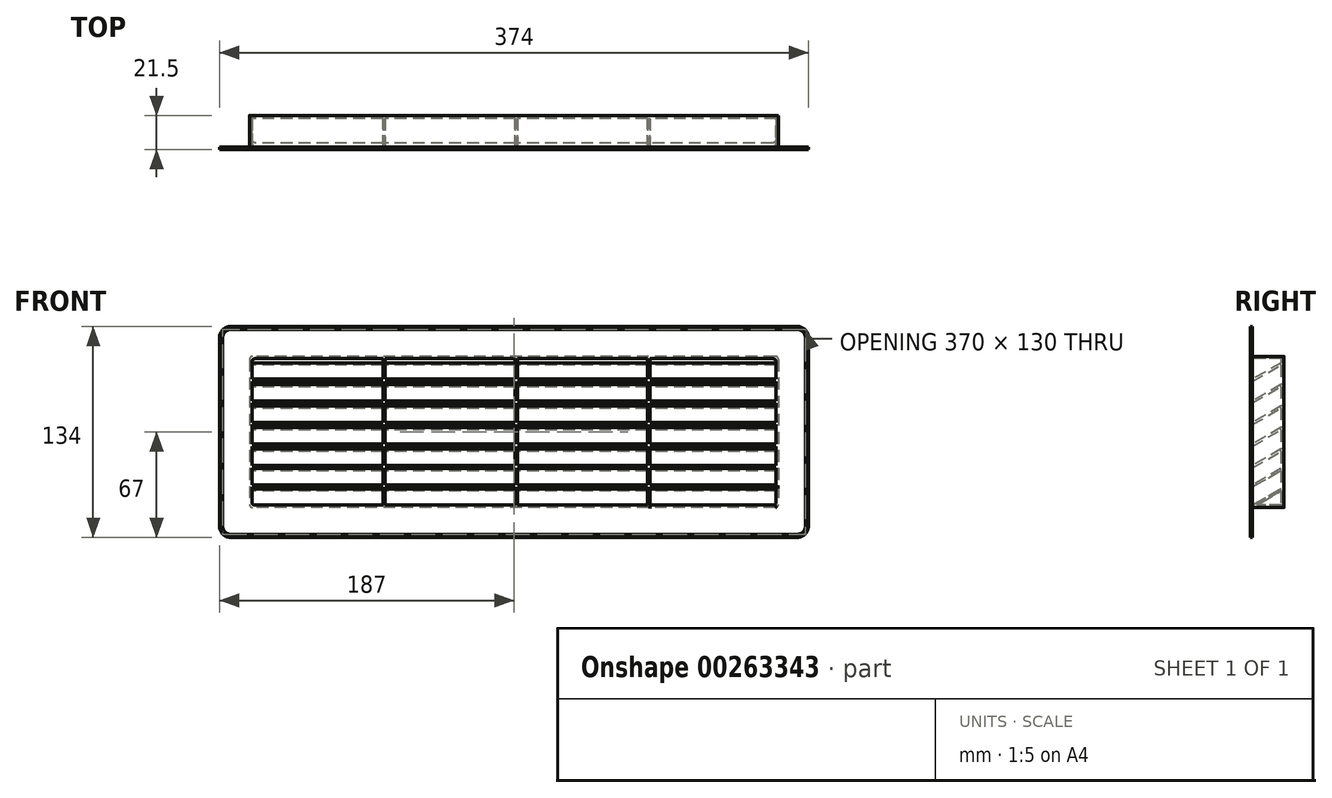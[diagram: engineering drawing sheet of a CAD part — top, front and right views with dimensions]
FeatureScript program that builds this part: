
annotation { "Feature Type Name" : "Feature", "Feature Type Description" : "" }
export const myFeature = defineFeature(function(context is Context, id is Id, definition is map)
    precondition{}
    {
        {
            var Q0;
            Q0=qCreatedBy(makeId("Front.planeOp"),FACE);
            var sketch = newSketch(context, id + "F0", { "sketchPlane" : qUnion([Q0])});
            skLineSegment(sketch, "E0.bottom", {"start": v(-180, 65) * mm, "end": v(180, 65) * mm});
            skLineSegment(sketch, "E0.top", {"start": v(-180, -65) * mm, "end": v(180, -65) * mm});
            skLineSegment(sketch, "E0.left", {"start": v(-185, 60) * mm, "end": v(-185, -60) * mm});
            skLineSegment(sketch, "E0.right", {"start": v(185, 60) * mm, "end": v(185, -60) * mm});
            skPoint(sketch, "E0.middle", {"position": v(0, 0) * mm});
            skPoint(sketch, "E1.visualSharp", {"position": v(-185, 65) * mm});
            skArc(sketch, "E1.filletArc", {"start": v(-180, 65) * mm, "mid": v(-183.54, 63.54) * mm, "end": v(-185, 60) * mm});
            skPoint(sketch, "E2.visualSharp", {"position": v(185, 65) * mm});
            skArc(sketch, "E2.filletArc", {"start": v(185, 60) * mm, "mid": v(183.54, 63.54) * mm, "end": v(180, 65) * mm});
            skPoint(sketch, "E3.visualSharp", {"position": v(185, -65) * mm});
            skArc(sketch, "E3.filletArc", {"start": v(180, -65) * mm, "mid": v(183.54, -63.54) * mm, "end": v(185, -60) * mm});
            skPoint(sketch, "E4.visualSharp", {"position": v(-185, -65) * mm});
            skArc(sketch, "E4.filletArc", {"start": v(-185, -60) * mm, "mid": v(-183.54, -63.54) * mm, "end": v(-180, -65) * mm});
            skSolve(sketch);
        }
        {
            var Q0;
            Q0 = qSketchRegion(id + "F0", true);
            extrude(context, id + "F1", {"entities" : qUnion([Q0]), "depth" : 1.5 * mm});
        }
        {
            var Q0;
            Q0=makeQuery(id+"F1.opExtrude","CAP_FACE",FACE,{"disambiguationData":[OSD([sQuery(id+"F0.wireOp",EDGE,"E0.bottom"),sQuery(id+"F0.wireOp",EDGE,"E0.top"),sQuery(id+"F0.wireOp",EDGE,"E0.left"),sQuery(id+"F0.wireOp",EDGE,"E0.right")])],"isStart":false});
            var sketch = newSketch(context, id + "F2", { "sketchPlane" : qUnion([Q0])});
            skLineSegment(sketch, "E5.bottom", {"start": v(-166.5, 46.5) * mm, "end": v(-83.25, 46.5) * mm});
            skLineSegment(sketch, "E5.top", {"start": v(-166.5, -46.5) * mm, "end": v(-83.25, -46.5) * mm});
            skLineSegment(sketch, "E5.left", {"start": v(-166.5, 46.5) * mm, "end": v(-166.5, 33.54) * mm});
            skLineSegment(sketch, "E5.right", {"start": v(166.5, 46.5) * mm, "end": v(166.5, 33.54) * mm});
            skPoint(sketch, "E5.middle", {"position": v(0, 0) * mm});
            skLineSegment(sketch, "E6.0", {"start": v(-166.5, 32.04) * mm, "end": v(-83.25, 32.04) * mm});
            skLineSegment(sketch, "E7.0", {"start": v(-166.5, 18.32) * mm, "end": v(-83.25, 18.32) * mm});
            skLineSegment(sketch, "E8.0", {"start": v(-166.5, 4.6) * mm, "end": v(-83.25, 4.6) * mm});
            skLineSegment(sketch, "E9.0", {"start": v(-166.5, -9.1) * mm, "end": v(-83.25, -9.1) * mm});
            skLineSegment(sketch, "E10.0", {"start": v(-166.5, -22.82) * mm, "end": v(-83.25, -22.82) * mm});
            skLineSegment(sketch, "E11.0", {"start": v(-166.5, -33.54) * mm, "end": v(-83.25, -33.54) * mm});
            skLineSegment(sketch, "E12.0", {"start": v(-166.5, 33.54) * mm, "end": v(-83.25, 33.54) * mm});
            skLineSegment(sketch, "E13.0", {"start": v(-166.5, 19.82) * mm, "end": v(-83.25, 19.82) * mm});
            skLineSegment(sketch, "E14.0", {"start": v(-166.5, 6.1) * mm, "end": v(-83.25, 6.1) * mm});
            skLineSegment(sketch, "E15.0", {"start": v(-166.5, -7.6) * mm, "end": v(-83.25, -7.6) * mm});
            skLineSegment(sketch, "E16.0", {"start": v(-166.5, -21.32) * mm, "end": v(-83.25, -21.32) * mm});
            skLineSegment(sketch, "E17.0", {"start": v(-166.5, -35.04) * mm, "end": v(-83.25, -35.04) * mm});
            skLineSegment(sketch, "E18.0", {"start": v(-83.25, 46.5) * mm, "end": v(-83.25, 33.54) * mm});
            skLineSegment(sketch, "E19.0", {"start": v(-81.75, 46.5) * mm, "end": v(-81.75, 33.54) * mm});
            skLineSegment(sketch, "E20.0", {"start": v(0.75, 46.5) * mm, "end": v(0.75, 33.54) * mm});
            skLineSegment(sketch, "E21.0", {"start": v(2.25, 46.5) * mm, "end": v(2.25, 33.54) * mm});
            skLineSegment(sketch, "E22.0", {"start": v(84.75, 46.5) * mm, "end": v(84.75, 33.54) * mm});
            skLineSegment(sketch, "E23.0", {"start": v(86.25, 46.5) * mm, "end": v(86.25, 33.54) * mm});
            skLineSegment(sketch, "E24.trimOffspring", {"start": v(-81.75, 19.82) * mm, "end": v(0.75, 19.82) * mm});
            skLineSegment(sketch, "E25.trimOffspring", {"start": v(-81.75, 18.32) * mm, "end": v(0.75, 18.32) * mm});
            skLineSegment(sketch, "E26.trimOffspring", {"start": v(-81.75, 33.54) * mm, "end": v(0.75, 33.54) * mm});
            skLineSegment(sketch, "E27.trimOffspring", {"start": v(-81.75, 32.04) * mm, "end": v(0.75, 32.04) * mm});
            skLineSegment(sketch, "E28.trimOffspring", {"start": v(-83.25, 32.04) * mm, "end": v(-83.25, 19.82) * mm});
            skLineSegment(sketch, "E29.trimOffspring", {"start": v(-81.75, 32.04) * mm, "end": v(-81.75, 19.82) * mm});
            skLineSegment(sketch, "E30.trimOffspring", {"start": v(-166.5, 32.04) * mm, "end": v(-166.5, 19.82) * mm});
            skLineSegment(sketch, "E31.trimOffspring", {"start": v(-166.5, 18.32) * mm, "end": v(-166.5, 6.1) * mm});
            skLineSegment(sketch, "E32.trimOffspring", {"start": v(-81.75, 18.32) * mm, "end": v(-81.75, 6.1) * mm});
            skLineSegment(sketch, "E33.trimOffspring", {"start": v(-83.25, 18.32) * mm, "end": v(-83.25, 6.1) * mm});
            skLineSegment(sketch, "E34.trimOffspring", {"start": v(-83.25, 4.6) * mm, "end": v(-83.25, -7.6) * mm});
            skLineSegment(sketch, "E35.trimOffspring", {"start": v(-81.75, 4.6) * mm, "end": v(-81.75, -7.6) * mm});
            skLineSegment(sketch, "E36.trimOffspring", {"start": v(-81.75, 4.6) * mm, "end": v(0.75, 4.6) * mm});
            skLineSegment(sketch, "E37.trimOffspring", {"start": v(-81.75, 6.1) * mm, "end": v(0.75, 6.1) * mm});
            skLineSegment(sketch, "E38.trimOffspring", {"start": v(-166.5, 4.6) * mm, "end": v(-166.5, -7.6) * mm});
            skLineSegment(sketch, "E39.trimOffspring", {"start": v(-166.5, -9.1) * mm, "end": v(-166.5, -21.32) * mm});
            skLineSegment(sketch, "E40.trimOffspring", {"start": v(-83.25, -9.1) * mm, "end": v(-83.25, -21.32) * mm});
            skLineSegment(sketch, "E41.trimOffspring", {"start": v(-81.75, -9.1) * mm, "end": v(-81.75, -21.32) * mm});
            skLineSegment(sketch, "E42.trimOffspring", {"start": v(-81.75, -7.6) * mm, "end": v(0.75, -7.6) * mm});
            skLineSegment(sketch, "E43.trimOffspring", {"start": v(-81.75, -9.1) * mm, "end": v(0.75, -9.1) * mm});
            skLineSegment(sketch, "E44.trimOffspring", {"start": v(-166.5, -22.82) * mm, "end": v(-166.5, -33.54) * mm});
            skLineSegment(sketch, "E45.trimOffspring", {"start": v(-166.5, -35.04) * mm, "end": v(-166.5, -46.5) * mm});
            skLineSegment(sketch, "E46.trimOffspring", {"start": v(-83.25, -22.82) * mm, "end": v(-83.25, -33.54) * mm});
            skLineSegment(sketch, "E47.trimOffspring", {"start": v(-81.75, -22.82) * mm, "end": v(0.75, -22.82) * mm});
            skLineSegment(sketch, "E48.trimOffspring", {"start": v(-81.75, -21.32) * mm, "end": v(0.75, -21.32) * mm});
            skLineSegment(sketch, "E49.trimOffspring", {"start": v(-81.75, -22.82) * mm, "end": v(-81.75, -33.54) * mm});
            skLineSegment(sketch, "E50.trimOffspring", {"start": v(-83.25, -35.04) * mm, "end": v(-83.25, -46.5) * mm});
            skLineSegment(sketch, "E51.trimOffspring", {"start": v(-81.75, -35.04) * mm, "end": v(0.75, -35.04) * mm});
            skLineSegment(sketch, "E52.trimOffspring", {"start": v(-81.75, -33.54) * mm, "end": v(0.75, -33.54) * mm});
            skLineSegment(sketch, "E53.trimOffspring", {"start": v(-81.75, -35.04) * mm, "end": v(-81.75, -46.5) * mm});
            skLineSegment(sketch, "E54.trimOffspring", {"start": v(-81.75, -46.5) * mm, "end": v(0.75, -46.5) * mm});
            skLineSegment(sketch, "E55.trimOffspring", {"start": v(-81.75, 46.5) * mm, "end": v(0.75, 46.5) * mm});
            skLineSegment(sketch, "E56.trimOffspring", {"start": v(2.25, 46.5) * mm, "end": v(84.75, 46.5) * mm});
            skLineSegment(sketch, "E57.trimOffspring", {"start": v(2.25, 32.04) * mm, "end": v(84.75, 32.04) * mm});
            skLineSegment(sketch, "E58.trimOffspring", {"start": v(2.25, 33.54) * mm, "end": v(84.75, 33.54) * mm});
            skLineSegment(sketch, "E59.trimOffspring", {"start": v(2.25, 32.04) * mm, "end": v(2.25, 19.82) * mm});
            skLineSegment(sketch, "E60.trimOffspring", {"start": v(0.75, 32.04) * mm, "end": v(0.75, 19.82) * mm});
            skLineSegment(sketch, "E61.trimOffspring", {"start": v(2.25, 19.82) * mm, "end": v(84.75, 19.82) * mm});
            skLineSegment(sketch, "E62.trimOffspring", {"start": v(2.25, 18.32) * mm, "end": v(2.25, 6.1) * mm});
            skLineSegment(sketch, "E63.trimOffspring", {"start": v(2.25, 18.32) * mm, "end": v(84.75, 18.32) * mm});
            skLineSegment(sketch, "E64.trimOffspring", {"start": v(0.75, 18.32) * mm, "end": v(0.75, 6.1) * mm});
            skLineSegment(sketch, "E65.trimOffspring", {"start": v(2.25, 4.6) * mm, "end": v(2.25, -7.6) * mm});
            skLineSegment(sketch, "E66.trimOffspring", {"start": v(2.25, 6.1) * mm, "end": v(84.75, 6.1) * mm});
            skLineSegment(sketch, "E67.trimOffspring", {"start": v(0.75, 4.6) * mm, "end": v(0.75, -7.6) * mm});
            skLineSegment(sketch, "E68.trimOffspring", {"start": v(2.25, 4.6) * mm, "end": v(84.75, 4.6) * mm});
            skLineSegment(sketch, "E69.trimOffspring", {"start": v(2.25, -7.6) * mm, "end": v(84.75, -7.6) * mm});
            skLineSegment(sketch, "E70.trimOffspring", {"start": v(0.75, -9.1) * mm, "end": v(0.75, -21.32) * mm});
            skLineSegment(sketch, "E71.trimOffspring", {"start": v(2.25, -9.1) * mm, "end": v(2.25, -21.32) * mm});
            skLineSegment(sketch, "E72.trimOffspring", {"start": v(2.25, -9.1) * mm, "end": v(84.75, -9.1) * mm});
            skLineSegment(sketch, "E73.trimOffspring", {"start": v(2.25, -22.82) * mm, "end": v(2.25, -33.54) * mm});
            skLineSegment(sketch, "E74.trimOffspring", {"start": v(2.25, -21.32) * mm, "end": v(84.75, -21.32) * mm});
            skLineSegment(sketch, "E75.trimOffspring", {"start": v(0.75, -22.82) * mm, "end": v(0.75, -33.54) * mm});
            skLineSegment(sketch, "E76.trimOffspring", {"start": v(2.25, -22.82) * mm, "end": v(84.75, -22.82) * mm});
            skLineSegment(sketch, "E77.trimOffspring", {"start": v(2.25, -35.04) * mm, "end": v(84.75, -35.04) * mm});
            skLineSegment(sketch, "E78.trimOffspring", {"start": v(2.25, -35.04) * mm, "end": v(2.25, -46.5) * mm});
            skLineSegment(sketch, "E79.trimOffspring", {"start": v(2.25, -33.54) * mm, "end": v(84.75, -33.54) * mm});
            skLineSegment(sketch, "E80.trimOffspring", {"start": v(0.75, -35.04) * mm, "end": v(0.75, -46.5) * mm});
            skLineSegment(sketch, "E81.trimOffspring", {"start": v(2.25, -46.5) * mm, "end": v(84.75, -46.5) * mm});
            skLineSegment(sketch, "E82.trimOffspring", {"start": v(86.25, 46.5) * mm, "end": v(166.5, 46.5) * mm});
            skLineSegment(sketch, "E83.trimOffspring", {"start": v(86.25, 33.54) * mm, "end": v(166.5, 33.54) * mm});
            skLineSegment(sketch, "E84.trimOffspring", {"start": v(84.75, 32.04) * mm, "end": v(84.75, 19.82) * mm});
            skLineSegment(sketch, "E85.trimOffspring", {"start": v(86.25, 32.04) * mm, "end": v(86.25, 19.82) * mm});
            skLineSegment(sketch, "E86.trimOffspring", {"start": v(86.25, 32.04) * mm, "end": v(166.5, 32.04) * mm});
            skLineSegment(sketch, "E87.trimOffspring", {"start": v(84.75, 4.6) * mm, "end": v(84.75, -7.6) * mm});
            skLineSegment(sketch, "E88.trimOffspring", {"start": v(86.25, 4.6) * mm, "end": v(86.25, -7.6) * mm});
            skLineSegment(sketch, "E89.trimOffspring", {"start": v(86.25, 6.1) * mm, "end": v(166.5, 6.1) * mm});
            skLineSegment(sketch, "E90.trimOffspring", {"start": v(86.25, 4.6) * mm, "end": v(166.5, 4.6) * mm});
            skLineSegment(sketch, "E91.trimOffspring", {"start": v(86.25, 18.32) * mm, "end": v(166.5, 18.32) * mm});
            skLineSegment(sketch, "E92.trimOffspring", {"start": v(86.25, 18.32) * mm, "end": v(86.25, 6.1) * mm});
            skLineSegment(sketch, "E93.trimOffspring", {"start": v(84.75, 18.32) * mm, "end": v(84.75, 6.1) * mm});
            skLineSegment(sketch, "E94.trimOffspring", {"start": v(86.25, 19.82) * mm, "end": v(166.5, 19.82) * mm});
            skLineSegment(sketch, "E95.trimOffspring", {"start": v(86.25, -22.82) * mm, "end": v(166.5, -22.82) * mm});
            skLineSegment(sketch, "E96.trimOffspring", {"start": v(86.25, -22.82) * mm, "end": v(86.25, -33.54) * mm});
            skLineSegment(sketch, "E97.trimOffspring", {"start": v(84.75, -22.82) * mm, "end": v(84.75, -33.54) * mm});
            skLineSegment(sketch, "E98.trimOffspring", {"start": v(86.25, -9.1) * mm, "end": v(86.25, -21.32) * mm});
            skLineSegment(sketch, "E99.trimOffspring", {"start": v(84.75, -9.1) * mm, "end": v(84.75, -21.32) * mm});
            skLineSegment(sketch, "E100.trimOffspring", {"start": v(86.25, -7.6) * mm, "end": v(166.5, -7.6) * mm});
            skLineSegment(sketch, "E101.trimOffspring", {"start": v(86.25, -9.1) * mm, "end": v(166.5, -9.1) * mm});
            skLineSegment(sketch, "E102.trimOffspring", {"start": v(86.25, -21.32) * mm, "end": v(166.5, -21.32) * mm});
            skLineSegment(sketch, "E103.trimOffspring", {"start": v(86.25, -35.04) * mm, "end": v(86.25, -46.5) * mm});
            skLineSegment(sketch, "E104.trimOffspring", {"start": v(86.25, -35.04) * mm, "end": v(166.5, -35.04) * mm});
            skLineSegment(sketch, "E105.trimOffspring", {"start": v(86.25, -33.54) * mm, "end": v(166.5, -33.54) * mm});
            skLineSegment(sketch, "E106.trimOffspring", {"start": v(84.75, -35.04) * mm, "end": v(84.75, -46.5) * mm});
            skLineSegment(sketch, "E107.trimOffspring", {"start": v(86.25, -46.5) * mm, "end": v(166.5, -46.5) * mm});
            skLineSegment(sketch, "E108.trimOffspring", {"start": v(166.5, -35.04) * mm, "end": v(166.5, -46.5) * mm});
            skLineSegment(sketch, "E109.trimOffspring", {"start": v(166.5, -22.82) * mm, "end": v(166.5, -33.54) * mm});
            skLineSegment(sketch, "E110.trimOffspring", {"start": v(166.5, 32.04) * mm, "end": v(166.5, 19.82) * mm});
            skLineSegment(sketch, "E111.trimOffspring", {"start": v(166.5, 18.32) * mm, "end": v(166.5, 6.1) * mm});
            skLineSegment(sketch, "E112.trimOffspring", {"start": v(166.5, 4.6) * mm, "end": v(166.5, -7.6) * mm});
            skLineSegment(sketch, "E113.trimOffspring", {"start": v(166.5, -9.1) * mm, "end": v(166.5, -21.32) * mm});
            skSolve(sketch);
        }
        {
            var Q0;
            Q0=makeQuery(id+"F2.imprint","IMPRINT",FACE,{"disambiguationData":[TD([[makeQuery(id+"F2.imprint","IMPRINT",EDGE,{"derivedFrom":sQuery(id+"F2.wireOp",EDGE,"E5.bottom")}),-1.0]])]});
            var Q1;
            Q1=makeQuery(id+"F2.imprint","IMPRINT",FACE,{"disambiguationData":[TD([[makeQuery(id+"F2.imprint","IMPRINT",EDGE,{"derivedFrom":sQuery(id+"F2.wireOp",EDGE,"E19.0")}),1.0]])]});
            var Q2;
            Q2=makeQuery(id+"F2.imprint","IMPRINT",FACE,{"disambiguationData":[TD([[makeQuery(id+"F2.imprint","IMPRINT",EDGE,{"derivedFrom":sQuery(id+"F2.wireOp",EDGE,"E21.0")}),1.0]])]});
            var Q3;
            Q3=makeQuery(id+"F2.imprint","IMPRINT",FACE,{"disambiguationData":[TD([[makeQuery(id+"F2.imprint","IMPRINT",EDGE,{"derivedFrom":sQuery(id+"F2.wireOp",EDGE,"E5.right")}),-1.0]])]});
            var Q4;
            Q4=makeQuery(id+"F2.imprint","IMPRINT",FACE,{"disambiguationData":[TD([[makeQuery(id+"F2.imprint","IMPRINT",EDGE,{"derivedFrom":sQuery(id+"F2.wireOp",EDGE,"E6.0")}),-1.0]])]});
            var Q5;
            Q5=makeQuery(id+"F2.imprint","IMPRINT",FACE,{"disambiguationData":[TD([[makeQuery(id+"F2.imprint","IMPRINT",EDGE,{"derivedFrom":sQuery(id+"F2.wireOp",EDGE,"E24.trimOffspring")}),1.0]])]});
            var Q6;
            Q6=makeQuery(id+"F2.imprint","IMPRINT",FACE,{"disambiguationData":[TD([[makeQuery(id+"F2.imprint","IMPRINT",EDGE,{"derivedFrom":sQuery(id+"F2.wireOp",EDGE,"E57.trimOffspring")}),-1.0]])]});
            var Q7;
            Q7=makeQuery(id+"F2.imprint","IMPRINT",FACE,{"disambiguationData":[TD([[makeQuery(id+"F2.imprint","IMPRINT",EDGE,{"derivedFrom":sQuery(id+"F2.wireOp",EDGE,"E85.trimOffspring")}),1.0]])]});
            var Q8;
            Q8=makeQuery(id+"F2.imprint","IMPRINT",FACE,{"disambiguationData":[TD([[makeQuery(id+"F2.imprint","IMPRINT",EDGE,{"derivedFrom":sQuery(id+"F2.wireOp",EDGE,"E7.0")}),-1.0]])]});
            var Q9;
            Q9=makeQuery(id+"F2.imprint","IMPRINT",FACE,{"disambiguationData":[TD([[makeQuery(id+"F2.imprint","IMPRINT",EDGE,{"derivedFrom":sQuery(id+"F2.wireOp",EDGE,"E25.trimOffspring")}),-1.0]])]});
            var Q10;
            Q10=makeQuery(id+"F2.imprint","IMPRINT",FACE,{"disambiguationData":[TD([[makeQuery(id+"F2.imprint","IMPRINT",EDGE,{"derivedFrom":sQuery(id+"F2.wireOp",EDGE,"E62.trimOffspring")}),1.0]])]});
            var Q11;
            Q11=makeQuery(id+"F2.imprint","IMPRINT",FACE,{"disambiguationData":[TD([[makeQuery(id+"F2.imprint","IMPRINT",EDGE,{"derivedFrom":sQuery(id+"F2.wireOp",EDGE,"E89.trimOffspring")}),1.0]])]});
            var Q12;
            Q12=makeQuery(id+"F2.imprint","IMPRINT",FACE,{"disambiguationData":[TD([[makeQuery(id+"F2.imprint","IMPRINT",EDGE,{"derivedFrom":sQuery(id+"F2.wireOp",EDGE,"E8.0")}),-1.0]])]});
            var Q13;
            Q13=makeQuery(id+"F2.imprint","IMPRINT",FACE,{"disambiguationData":[TD([[makeQuery(id+"F2.imprint","IMPRINT",EDGE,{"derivedFrom":sQuery(id+"F2.wireOp",EDGE,"E35.trimOffspring")}),1.0]])]});
            var Q14;
            Q14=makeQuery(id+"F2.imprint","IMPRINT",FACE,{"disambiguationData":[TD([[makeQuery(id+"F2.imprint","IMPRINT",EDGE,{"derivedFrom":sQuery(id+"F2.wireOp",EDGE,"E65.trimOffspring")}),1.0]])]});
            var Q15;
            Q15=makeQuery(id+"F2.imprint","IMPRINT",FACE,{"disambiguationData":[TD([[makeQuery(id+"F2.imprint","IMPRINT",EDGE,{"derivedFrom":sQuery(id+"F2.wireOp",EDGE,"E88.trimOffspring")}),1.0]])]});
            var Q16;
            Q16=makeQuery(id+"F2.imprint","IMPRINT",FACE,{"disambiguationData":[TD([[makeQuery(id+"F2.imprint","IMPRINT",EDGE,{"derivedFrom":sQuery(id+"F2.wireOp",EDGE,"E9.0")}),-1.0]])]});
            var Q17;
            Q17=makeQuery(id+"F2.imprint","IMPRINT",FACE,{"disambiguationData":[TD([[makeQuery(id+"F2.imprint","IMPRINT",EDGE,{"derivedFrom":sQuery(id+"F2.wireOp",EDGE,"E41.trimOffspring")}),1.0]])]});
            var Q18;
            Q18=makeQuery(id+"F2.imprint","IMPRINT",FACE,{"disambiguationData":[TD([[makeQuery(id+"F2.imprint","IMPRINT",EDGE,{"derivedFrom":sQuery(id+"F2.wireOp",EDGE,"E71.trimOffspring")}),1.0]])]});
            var Q19;
            Q19=makeQuery(id+"F2.imprint","IMPRINT",FACE,{"disambiguationData":[TD([[makeQuery(id+"F2.imprint","IMPRINT",EDGE,{"derivedFrom":sQuery(id+"F2.wireOp",EDGE,"E98.trimOffspring")}),1.0]])]});
            var Q20;
            Q20=makeQuery(id+"F2.imprint","IMPRINT",FACE,{"disambiguationData":[TD([[makeQuery(id+"F2.imprint","IMPRINT",EDGE,{"derivedFrom":sQuery(id+"F2.wireOp",EDGE,"E10.0")}),-1.0]])]});
            var Q21;
            Q21=makeQuery(id+"F2.imprint","IMPRINT",FACE,{"disambiguationData":[TD([[makeQuery(id+"F2.imprint","IMPRINT",EDGE,{"derivedFrom":sQuery(id+"F2.wireOp",EDGE,"E47.trimOffspring")}),-1.0]])]});
            var Q22;
            Q22=makeQuery(id+"F2.imprint","IMPRINT",FACE,{"disambiguationData":[TD([[makeQuery(id+"F2.imprint","IMPRINT",EDGE,{"derivedFrom":sQuery(id+"F2.wireOp",EDGE,"E73.trimOffspring")}),1.0]])]});
            var Q23;
            Q23=makeQuery(id+"F2.imprint","IMPRINT",FACE,{"disambiguationData":[TD([[makeQuery(id+"F2.imprint","IMPRINT",EDGE,{"derivedFrom":sQuery(id+"F2.wireOp",EDGE,"E95.trimOffspring")}),-1.0]])]});
            var Q24;
            Q24=makeQuery(id+"F2.imprint","IMPRINT",FACE,{"disambiguationData":[TD([[makeQuery(id+"F2.imprint","IMPRINT",EDGE,{"derivedFrom":sQuery(id+"F2.wireOp",EDGE,"E5.top")}),1.0]])]});
            var Q25;
            Q25=makeQuery(id+"F2.imprint","IMPRINT",FACE,{"disambiguationData":[TD([[makeQuery(id+"F2.imprint","IMPRINT",EDGE,{"derivedFrom":sQuery(id+"F2.wireOp",EDGE,"E51.trimOffspring")}),-1.0]])]});
            var Q26;
            Q26=makeQuery(id+"F2.imprint","IMPRINT",FACE,{"disambiguationData":[TD([[makeQuery(id+"F2.imprint","IMPRINT",EDGE,{"derivedFrom":sQuery(id+"F2.wireOp",EDGE,"E77.trimOffspring")}),-1.0]])]});
            var Q27;
            Q27=makeQuery(id+"F2.imprint","IMPRINT",FACE,{"disambiguationData":[TD([[makeQuery(id+"F2.imprint","IMPRINT",EDGE,{"derivedFrom":sQuery(id+"F2.wireOp",EDGE,"E103.trimOffspring")}),1.0]])]});
            extrude(context, id + "F3", {"entities" : qUnion([Q0, Q1, Q2, Q3, Q4, Q5, Q6, Q7, Q8, Q9, Q10, Q11, Q12, Q13, Q14, Q15, Q16, Q17, Q18, Q19, Q20, Q21, Q22, Q23, Q24, Q25, Q26, Q27]), "operationType" : NewBodyOperationType.REMOVE, "endBound" : BoundingType.THROUGH_ALL, "oppositeDirection" : true, "depth" : 25 * mm});
        }
        {
            var Q0;
            Q0=makeQuery(id+"F1.opExtrude","CAP_FACE",FACE,{"disambiguationData":[OSD([sQuery(id+"F0.wireOp",EDGE,"E0.bottom"),sQuery(id+"F0.wireOp",EDGE,"E0.top"),sQuery(id+"F0.wireOp",EDGE,"E0.left"),sQuery(id+"F0.wireOp",EDGE,"E0.right")])],"isStart":true});
            var sketch = newSketch(context, id + "F4", { "sketchPlane" : qUnion([Q0])});
            skLineSegment(sketch, "E114.bottom", {"start": v(-166.5, 46.5) * mm, "end": v(166.5, 46.5) * mm});
            skLineSegment(sketch, "E114.top", {"start": v(-166.5, -46.5) * mm, "end": v(166.5, -46.5) * mm});
            skLineSegment(sketch, "E114.left", {"start": v(-166.5, 46.5) * mm, "end": v(-166.5, -46.5) * mm});
            skLineSegment(sketch, "E114.right", {"start": v(166.5, 46.5) * mm, "end": v(166.5, -46.5) * mm});
            skPoint(sketch, "E114.middle", {"position": v(0, 0) * mm});
            skLineSegment(sketch, "E115.0", {"start": v(-168, 48) * mm, "end": v(168, 48) * mm});
            skLineSegment(sketch, "E115.1", {"start": v(-168, 48) * mm, "end": v(-168, -48) * mm});
            skLineSegment(sketch, "E115.2", {"start": v(-168, -48) * mm, "end": v(168, -48) * mm});
            skLineSegment(sketch, "E115.3", {"start": v(168, 48) * mm, "end": v(168, -48) * mm});
            skSolve(sketch);
        }
        {
            var Q0;
            Q0 = qSketchRegion(id + "F4", true);
            extrude(context, id + "F5", {"entities" : qUnion([Q0]), "operationType" : NewBodyOperationType.ADD, "depth" : 20 * mm});
        }
        {
            var Q0;
            Q0=makeQuery(id+"F5.boolean.opBoolean","MERGE",FACE,{"derivedFrom":[makeQuery(id+"F3.boolean.opBoolean","COPY",FACE,{"derivedFrom":makeQuery(id+"F3.opExtrude","SWEPT_FACE",FACE,{"disambiguationData":[OSD([sQuery(id+"F2.wireOp",EDGE,"E5.left")])]})}),makeQuery(id+"F3.boolean.opBoolean","COPY",FACE,{"derivedFrom":makeQuery(id+"F3.opExtrude","SWEPT_FACE",FACE,{"disambiguationData":[OSD([sQuery(id+"F2.wireOp",EDGE,"E30.trimOffspring")])]})}),makeQuery(id+"F3.boolean.opBoolean","COPY",FACE,{"derivedFrom":makeQuery(id+"F3.opExtrude","SWEPT_FACE",FACE,{"disambiguationData":[OSD([sQuery(id+"F2.wireOp",EDGE,"E31.trimOffspring")])]})}),makeQuery(id+"F3.boolean.opBoolean","COPY",FACE,{"derivedFrom":makeQuery(id+"F3.opExtrude","SWEPT_FACE",FACE,{"disambiguationData":[OSD([sQuery(id+"F2.wireOp",EDGE,"E38.trimOffspring")])]})}),makeQuery(id+"F3.boolean.opBoolean","COPY",FACE,{"derivedFrom":makeQuery(id+"F3.opExtrude","SWEPT_FACE",FACE,{"disambiguationData":[OSD([sQuery(id+"F2.wireOp",EDGE,"E39.trimOffspring")])]})}),makeQuery(id+"F3.boolean.opBoolean","COPY",FACE,{"derivedFrom":makeQuery(id+"F3.opExtrude","SWEPT_FACE",FACE,{"disambiguationData":[OSD([sQuery(id+"F2.wireOp",EDGE,"E44.trimOffspring")])]})}),makeQuery(id+"F3.boolean.opBoolean","COPY",FACE,{"derivedFrom":makeQuery(id+"F3.opExtrude","SWEPT_FACE",FACE,{"disambiguationData":[OSD([sQuery(id+"F2.wireOp",EDGE,"E45.trimOffspring")])]})}),makeQuery(id+"F5.opExtrude","SWEPT_FACE",FACE,{"disambiguationData":[OSD([sQuery(id+"F4.wireOp",EDGE,"E114.right")])]})]});
            var sketch = newSketch(context, id + "F6", { "sketchPlane" : qUnion([Q0])});
            skLineSegment(sketch, "E116", {"start": v(0, 46.5) * mm, "end": v(0, -35.04) * mm, "construction": true});
            skPoint(sketch, "E116.endSnap0", {"position": v(0, 19.07) * mm});
            skLineSegment(sketch, "E117", {"start": v(0, 33.54) * mm, "end": v(18, 43.93) * mm});
            skLineSegment(sketch, "E118", {"start": v(18, 43.93) * mm, "end": v(18, 42.43) * mm});
            skLineSegment(sketch, "E119", {"start": v(18, 42.43) * mm, "end": v(0, 32.04) * mm});
            skLineSegment(sketch, "E120", {"start": v(0, 32.04) * mm, "end": v(0, 33.54) * mm});
            skLineSegment(sketch, "E121", {"start": v(0, 33.54) * mm, "end": v(0, 32.04) * mm});
            skLineSegment(sketch, "E122.0.1.0", {"start": v(0, 19.82) * mm, "end": v(18, 30.21) * mm});
            skLineSegment(sketch, "E122.0.1.1", {"start": v(18, 28.71) * mm, "end": v(0, 18.32) * mm});
            skLineSegment(sketch, "E122.0.1.2", {"start": v(18, 30.21) * mm, "end": v(18, 28.71) * mm});
            skLineSegment(sketch, "E122.0.2.0", {"start": v(0, 6.1) * mm, "end": v(18, 16.5) * mm});
            skLineSegment(sketch, "E122.0.2.1", {"start": v(18, 15) * mm, "end": v(0, 4.6) * mm});
            skLineSegment(sketch, "E122.0.2.2", {"start": v(18, 16.5) * mm, "end": v(18, 15) * mm});
            skLineSegment(sketch, "E122.0.3.0", {"start": v(0, -7.6) * mm, "end": v(18, 2.79) * mm});
            skLineSegment(sketch, "E122.0.3.1", {"start": v(18, 1.29) * mm, "end": v(0, -9.1) * mm});
            skLineSegment(sketch, "E122.0.3.2", {"start": v(18, 2.79) * mm, "end": v(18, 1.29) * mm});
            skLineSegment(sketch, "E122.0.4.0", {"start": v(0, -21.32) * mm, "end": v(18, -10.93) * mm});
            skLineSegment(sketch, "E122.0.4.1", {"start": v(18, -12.43) * mm, "end": v(0, -22.82) * mm});
            skLineSegment(sketch, "E122.0.4.2", {"start": v(18, -10.93) * mm, "end": v(18, -12.43) * mm});
            skLineSegment(sketch, "E122.0.5.0", {"start": v(0, -35.04) * mm, "end": v(18, -24.64) * mm});
            skLineSegment(sketch, "E122.direction1", {"start": v(0, 33.54) * mm, "end": v(0, 33.54) * mm});
            skLineSegment(sketch, "E122.direction2", {"start": v(0, 33.54) * mm, "end": v(0, 19.82) * mm, "construction": true});
            skLineSegment(sketch, "E123", {"start": v(0, 19.82) * mm, "end": v(0, 18.32) * mm});
            skLineSegment(sketch, "E124", {"start": v(0, 6.1) * mm, "end": v(0, 4.6) * mm});
            skLineSegment(sketch, "E125", {"start": v(0, -33.54) * mm, "end": v(18, -23.14) * mm});
            skLineSegment(sketch, "E126", {"start": v(18, -23.14) * mm, "end": v(18, -24.64) * mm});
            skLineSegment(sketch, "E127.trimOffspring", {"start": v(0, -35.04) * mm, "end": v(0, -46.5) * mm, "construction": true});
            skLineSegment(sketch, "E128", {"start": v(0, -35.04) * mm, "end": v(0, -33.54) * mm});
            skLineSegment(sketch, "E129", {"start": v(0, -21.32) * mm, "end": v(0, -22.82) * mm});
            skLineSegment(sketch, "E130", {"start": v(0, -46.5) * mm, "end": v(18, -36.1) * mm});
            skLineSegment(sketch, "E131", {"start": v(18, -36.1) * mm, "end": v(18, -37.6) * mm});
            skLineSegment(sketch, "E132", {"start": v(18, -37.6) * mm, "end": v(2.6, -46.5) * mm});
            skLineSegment(sketch, "E133", {"start": v(2.6, -46.5) * mm, "end": v(0, -46.5) * mm});
            skLineSegment(sketch, "E134", {"start": v(0, -7.6) * mm, "end": v(0, -9.1) * mm});
            skSolve(sketch);
        }
        {
            var Q0;
            Q0=makeQuery(id+"F5.boolean.opBoolean","SPLIT",FACE,{"disambiguationData":[TD([makeQuery(id+"F3.boolean.opBoolean","COPY",FACE,{"derivedFrom":makeQuery(id+"F3.opExtrude","SWEPT_FACE",FACE,{"disambiguationData":[OSD([sQuery(id+"F2.wireOp",EDGE,"E5.bottom")])]})})])],"derivedFrom":makeQuery(id+"F1.opExtrude","CAP_FACE",FACE,{"disambiguationData":[OSD([sQuery(id+"F0.wireOp",EDGE,"E0.bottom"),sQuery(id+"F0.wireOp",EDGE,"E0.top"),sQuery(id+"F0.wireOp",EDGE,"E0.left"),sQuery(id+"F0.wireOp",EDGE,"E0.right")])],"isStart":true})});
            var sketch = newSketch(context, id + "F7", { "sketchPlane" : qUnion([Q0])});
            skLineSegment(sketch, "E135.bottom", {"start": v(-86.25, 46.5) * mm, "end": v(-84.75, 46.5) * mm});
            skLineSegment(sketch, "E135.top", {"start": v(-86.25, -46.5) * mm, "end": v(-84.75, -46.5) * mm});
            skLineSegment(sketch, "E135.left", {"start": v(-86.25, 46.5) * mm, "end": v(-86.25, -46.5) * mm});
            skLineSegment(sketch, "E135.right", {"start": v(-84.75, 46.5) * mm, "end": v(-84.75, -46.5) * mm});
            skLineSegment(sketch, "E136.bottom", {"start": v(-2.25, 46.5) * mm, "end": v(-0.75, 46.5) * mm});
            skLineSegment(sketch, "E136.top", {"start": v(-2.25, -46.5) * mm, "end": v(-0.75, -46.5) * mm});
            skLineSegment(sketch, "E136.left", {"start": v(-2.25, 46.5) * mm, "end": v(-2.25, -46.5) * mm});
            skLineSegment(sketch, "E136.right", {"start": v(-0.75, 46.5) * mm, "end": v(-0.75, -46.5) * mm});
            skLineSegment(sketch, "E137.bottom", {"start": v(81.75, 46.5) * mm, "end": v(83.25, 46.5) * mm});
            skLineSegment(sketch, "E137.top", {"start": v(81.75, -46.5) * mm, "end": v(83.25, -46.5) * mm});
            skLineSegment(sketch, "E137.left", {"start": v(81.75, 46.5) * mm, "end": v(81.75, -46.5) * mm});
            skLineSegment(sketch, "E137.right", {"start": v(83.25, 46.5) * mm, "end": v(83.25, -46.5) * mm});
            skSolve(sketch);
        }
        {
            var Q0;
            Q0 = qSketchRegion(id + "F7", true);
            extrude(context, id + "F8", {"entities" : qUnion([Q0]), "operationType" : NewBodyOperationType.ADD, "depth" : 18 * mm});
        }
        {
            var Q0;
            Q0 = qSketchRegion(id + "F6", true);
            var Q1;
            Q1=makeQuery(id+"F5.boolean.opBoolean","MERGE",FACE,{"derivedFrom":[makeQuery(id+"F3.boolean.opBoolean","COPY",FACE,{"derivedFrom":makeQuery(id+"F3.opExtrude","SWEPT_FACE",FACE,{"disambiguationData":[OSD([sQuery(id+"F2.wireOp",EDGE,"E5.right")])]})}),makeQuery(id+"F3.boolean.opBoolean","COPY",FACE,{"derivedFrom":makeQuery(id+"F3.opExtrude","SWEPT_FACE",FACE,{"disambiguationData":[OSD([sQuery(id+"F2.wireOp",EDGE,"E108.trimOffspring")])]})}),makeQuery(id+"F3.boolean.opBoolean","COPY",FACE,{"derivedFrom":makeQuery(id+"F3.opExtrude","SWEPT_FACE",FACE,{"disambiguationData":[OSD([sQuery(id+"F2.wireOp",EDGE,"E109.trimOffspring")])]})}),makeQuery(id+"F3.boolean.opBoolean","COPY",FACE,{"derivedFrom":makeQuery(id+"F3.opExtrude","SWEPT_FACE",FACE,{"disambiguationData":[OSD([sQuery(id+"F2.wireOp",EDGE,"E110.trimOffspring")])]})}),makeQuery(id+"F3.boolean.opBoolean","COPY",FACE,{"derivedFrom":makeQuery(id+"F3.opExtrude","SWEPT_FACE",FACE,{"disambiguationData":[OSD([sQuery(id+"F2.wireOp",EDGE,"E111.trimOffspring")])]})}),makeQuery(id+"F3.boolean.opBoolean","COPY",FACE,{"derivedFrom":makeQuery(id+"F3.opExtrude","SWEPT_FACE",FACE,{"disambiguationData":[OSD([sQuery(id+"F2.wireOp",EDGE,"E112.trimOffspring")])]})}),makeQuery(id+"F3.boolean.opBoolean","COPY",FACE,{"derivedFrom":makeQuery(id+"F3.opExtrude","SWEPT_FACE",FACE,{"disambiguationData":[OSD([sQuery(id+"F2.wireOp",EDGE,"E113.trimOffspring")])]})}),makeQuery(id+"F5.opExtrude","SWEPT_FACE",FACE,{"disambiguationData":[OSD([sQuery(id+"F4.wireOp",EDGE,"E114.left")])]})]});
            extrude(context, id + "F9", {"entities" : qUnion([Q0]), "operationType" : NewBodyOperationType.ADD, "endBound" : BoundingType.UP_TO_SURFACE, "endBoundEntityFace" : qUnion([Q1]), "depth" : 25 * mm});
        }
        {
            var Q0;
            Q0=makeQuery(id+"F5.opExtrude","SWEPT_EDGE",EDGE,{"disambiguationData":[OSD([sQuery(id+"F4.wireOp",EDGE,"E115.1"),sQuery(id+"F4.wireOp",EDGE,"E115.2")])]});
            var Q1;
            Q1=makeQuery(id+"F5.opExtrude","SWEPT_EDGE",EDGE,{"disambiguationData":[OSD([sQuery(id+"F4.wireOp",EDGE,"E115.0"),sQuery(id+"F4.wireOp",EDGE,"E115.1")])]});
            var Q2;
            Q2=makeQuery(id+"F5.opExtrude","SWEPT_EDGE",EDGE,{"disambiguationData":[OSD([sQuery(id+"F4.wireOp",EDGE,"E115.2"),sQuery(id+"F4.wireOp",EDGE,"E115.3")])]});
            var Q3;
            Q3=makeQuery(id+"F5.opExtrude","SWEPT_EDGE",EDGE,{"disambiguationData":[OSD([sQuery(id+"F4.wireOp",EDGE,"E115.0"),sQuery(id+"F4.wireOp",EDGE,"E115.3")])]});
            fillet(context, id + "F10", {"entities" : qUnion([Q0, Q1, Q2, Q3]), "radius" : 2 * mm, "tangentPropagation" : true, "allowEdgeOverflow" : false});
        }
        {
            var Q0;
            Q0=makeQuery(id+"F5.boolean.opBoolean","MERGE",EDGE,{"derivedFrom":[makeQuery(id+"F3.boolean.opBoolean","COPY",EDGE,{"derivedFrom":makeQuery(id+"F3.opExtrude","SWEPT_EDGE",EDGE,{"disambiguationData":[OSD([sQuery(id+"F2.wireOp",EDGE,"E5.bottom"),sQuery(id+"F2.wireOp",EDGE,"E5.left")])]})}),makeQuery(id+"F5.opExtrude","SWEPT_EDGE",EDGE,{"disambiguationData":[OSD([sQuery(id+"F4.wireOp",EDGE,"E114.bottom"),sQuery(id+"F4.wireOp",EDGE,"E114.right")])]})]});
            fillet(context, id + "F11", {"entities" : qUnion([Q0]), "radius" : 2 * mm, "tangentPropagation" : true, "allowEdgeOverflow" : false});
        }
        {
            var Q0;
            {var subQ0=sQuery(id+"F2.wireOp",EDGE,"E45.trimOffspring");var subQ1=sQuery(id+"F2.wireOp",EDGE,"E5.top");var subQ2=sQuery(id+"F4.wireOp",EDGE,"E114.right");var subQ3=sQuery(id+"F4.wireOp",EDGE,"E114.top");Q0=makeQuery(id+"F9.boolean.opBoolean","SPLIT",EDGE,{"disambiguationData":[TD([makeQuery(id+"F9.opExtrude","SWEPT_FACE",FACE,{"disambiguationData":[OSD([sQuery(id+"F6.wireOp",EDGE,"E132")])]})])],"derivedFrom":makeQuery(id+"F5.boolean.opBoolean","MERGE",EDGE,{"derivedFrom":[makeQuery(id+"F3.boolean.opBoolean","COPY",EDGE,{"derivedFrom":makeQuery(id+"F3.opExtrude","SWEPT_EDGE",EDGE,{"disambiguationData":[OSD([subQ1,subQ0])]})}),makeQuery(id+"F5.opExtrude","SWEPT_EDGE",EDGE,{"disambiguationData":[OSD([subQ3,subQ2])]})]})});}
            var Q1;
            {var subQ0=sQuery(id+"F2.wireOp",EDGE,"E108.trimOffspring");var subQ1=sQuery(id+"F2.wireOp",EDGE,"E107.trimOffspring");var subQ2=sQuery(id+"F4.wireOp",EDGE,"E114.left");var subQ3=sQuery(id+"F4.wireOp",EDGE,"E114.top");Q1=makeQuery(id+"F9.boolean.opBoolean","SPLIT",EDGE,{"disambiguationData":[TD([makeQuery(id+"F9.opExtrude","SWEPT_FACE",FACE,{"disambiguationData":[OSD([sQuery(id+"F6.wireOp",EDGE,"E132")])]})])],"derivedFrom":makeQuery(id+"F5.boolean.opBoolean","MERGE",EDGE,{"derivedFrom":[makeQuery(id+"F3.boolean.opBoolean","COPY",EDGE,{"derivedFrom":makeQuery(id+"F3.opExtrude","SWEPT_EDGE",EDGE,{"disambiguationData":[OSD([subQ1,subQ0])]})}),makeQuery(id+"F5.opExtrude","SWEPT_EDGE",EDGE,{"disambiguationData":[OSD([subQ3,subQ2])]})]})});}
            var Q2;
            Q2=makeQuery(id+"F5.boolean.opBoolean","MERGE",EDGE,{"derivedFrom":[makeQuery(id+"F3.boolean.opBoolean","COPY",EDGE,{"derivedFrom":makeQuery(id+"F3.opExtrude","SWEPT_EDGE",EDGE,{"disambiguationData":[OSD([sQuery(id+"F2.wireOp",EDGE,"E5.right"),sQuery(id+"F2.wireOp",EDGE,"E82.trimOffspring")])]})}),makeQuery(id+"F5.opExtrude","SWEPT_EDGE",EDGE,{"disambiguationData":[OSD([sQuery(id+"F4.wireOp",EDGE,"E114.bottom"),sQuery(id+"F4.wireOp",EDGE,"E114.left")])]})]});
            fillet(context, id + "F12", {"entities" : qUnion([Q0, Q1, Q2]), "radius" : 2 * mm, "tangentPropagation" : true, "allowEdgeOverflow" : false});
        }
        {
            var Q0;
            {var subQ0=sQuery(id+"F2.wireOp",EDGE,"E45.trimOffspring");var subQ1=sQuery(id+"F4.wireOp",EDGE,"E114.right");var subQ2=sQuery(id+"F2.wireOp",EDGE,"E5.top");var subQ3=sQuery(id+"F4.wireOp",EDGE,"E114.top");Q0=makeQuery(id+"F9.boolean.opBoolean","SPLIT",EDGE,{"disambiguationData":[TD([makeQuery(id+"F9.opExtrude","SWEPT_FACE",FACE,{"disambiguationData":[OSD([sQuery(id+"F6.wireOp",EDGE,"E130")])]})])],"derivedFrom":makeQuery(id+"F5.boolean.opBoolean","MERGE",EDGE,{"derivedFrom":[makeQuery(id+"F3.boolean.opBoolean","COPY",EDGE,{"derivedFrom":makeQuery(id+"F3.opExtrude","SWEPT_EDGE",EDGE,{"disambiguationData":[OSD([subQ2,subQ0])]})}),makeQuery(id+"F5.opExtrude","SWEPT_EDGE",EDGE,{"disambiguationData":[OSD([subQ3,subQ1])]})]})});}
            var Q1;
            {var subQ0=sQuery(id+"F2.wireOp",EDGE,"E108.trimOffspring");var subQ1=sQuery(id+"F2.wireOp",EDGE,"E107.trimOffspring");var subQ2=sQuery(id+"F4.wireOp",EDGE,"E114.top");var subQ3=sQuery(id+"F4.wireOp",EDGE,"E114.left");Q1=makeQuery(id+"F9.boolean.opBoolean","SPLIT",EDGE,{"disambiguationData":[TD([makeQuery(id+"F9.opExtrude","SWEPT_FACE",FACE,{"disambiguationData":[OSD([sQuery(id+"F6.wireOp",EDGE,"E130")])]})])],"derivedFrom":makeQuery(id+"F5.boolean.opBoolean","MERGE",EDGE,{"derivedFrom":[makeQuery(id+"F3.boolean.opBoolean","COPY",EDGE,{"derivedFrom":makeQuery(id+"F3.opExtrude","SWEPT_EDGE",EDGE,{"disambiguationData":[OSD([subQ1,subQ0])]})}),makeQuery(id+"F5.opExtrude","SWEPT_EDGE",EDGE,{"disambiguationData":[OSD([subQ2,subQ3])]})]})});}
            fillet(context, id + "F13", {"entities" : qUnion([Q0, Q1]), "radius" : 2 * mm, "tangentPropagation" : true, "allowEdgeOverflow" : false});
        }
        {
            var Q0;
            Q0=makeQuery(id+"F3.boolean.opBoolean","COPY",EDGE,{"derivedFrom":makeQuery(id+"F3.opExtrude","CAP_EDGE",EDGE,{"disambiguationData":[OSD([sQuery(id+"F2.wireOp",EDGE,"E55.trimOffspring")])],"isStart":true})});
            var Q1;
            Q1=makeQuery(id+"F3.boolean.opBoolean","COPY",EDGE,{"derivedFrom":makeQuery(id+"F3.opExtrude","CAP_EDGE",EDGE,{"disambiguationData":[OSD([sQuery(id+"F2.wireOp",EDGE,"E56.trimOffspring")])],"isStart":true})});
            var Q2;
            Q2=makeQuery(id+"F3.boolean.opBoolean","COPY",EDGE,{"derivedFrom":makeQuery(id+"F3.opExtrude","CAP_EDGE",EDGE,{"disambiguationData":[OSD([sQuery(id+"F2.wireOp",EDGE,"E82.trimOffspring")])],"isStart":true})});
            var Q3;
            Q3=makeQuery(id+"F3.boolean.opBoolean","COPY",EDGE,{"derivedFrom":makeQuery(id+"F3.opExtrude","CAP_EDGE",EDGE,{"disambiguationData":[OSD([sQuery(id+"F2.wireOp",EDGE,"E110.trimOffspring")])],"isStart":true})});
            var Q4;
            Q4=makeQuery(id+"F3.boolean.opBoolean","COPY",EDGE,{"derivedFrom":makeQuery(id+"F3.opExtrude","CAP_EDGE",EDGE,{"disambiguationData":[OSD([sQuery(id+"F2.wireOp",EDGE,"E111.trimOffspring")])],"isStart":true})});
            var Q5;
            Q5=makeQuery(id+"F3.boolean.opBoolean","COPY",EDGE,{"derivedFrom":makeQuery(id+"F3.opExtrude","CAP_EDGE",EDGE,{"disambiguationData":[OSD([sQuery(id+"F2.wireOp",EDGE,"E112.trimOffspring")])],"isStart":true})});
            var Q6;
            Q6=makeQuery(id+"F3.boolean.opBoolean","COPY",EDGE,{"derivedFrom":makeQuery(id+"F3.opExtrude","CAP_EDGE",EDGE,{"disambiguationData":[OSD([sQuery(id+"F2.wireOp",EDGE,"E113.trimOffspring")])],"isStart":true})});
            var Q7;
            Q7=makeQuery(id+"F3.boolean.opBoolean","COPY",EDGE,{"derivedFrom":makeQuery(id+"F3.opExtrude","CAP_EDGE",EDGE,{"disambiguationData":[OSD([sQuery(id+"F2.wireOp",EDGE,"E109.trimOffspring")])],"isStart":true})});
            var Q8;
            Q8=makeQuery(id+"F3.boolean.opBoolean","COPY",EDGE,{"derivedFrom":makeQuery(id+"F3.opExtrude","CAP_EDGE",EDGE,{"disambiguationData":[OSD([sQuery(id+"F2.wireOp",EDGE,"E108.trimOffspring")])],"isStart":true})});
            var Q9;
            {var subQ0=makeQuery(id+"F1.opExtrude","CAP_FACE",FACE,{"disambiguationData":[OSD([sQuery(id+"F0.wireOp",EDGE,"E0.bottom"),sQuery(id+"F0.wireOp",EDGE,"E0.top"),sQuery(id+"F0.wireOp",EDGE,"E0.left"),sQuery(id+"F0.wireOp",EDGE,"E0.right"),sQuery(id+"F0.wireOp",EDGE,"E1.filletArc"),sQuery(id+"F0.wireOp",EDGE,"E2.filletArc"),sQuery(id+"F0.wireOp",EDGE,"E3.filletArc"),sQuery(id+"F0.wireOp",EDGE,"E4.filletArc")])],"isStart":false});var subQ1=sQuery(id+"F2.wireOp",EDGE,"E108.trimOffspring");var subQ2=sQuery(id+"F2.wireOp",EDGE,"E107.trimOffspring");var subQ3=sQuery(id+"F4.wireOp",EDGE,"E114.top");var subQ4=sQuery(id+"F4.wireOp",EDGE,"E114.left");Q9=makeQuery(id+"F13.opFillet","BLEND_EDGE",EDGE,{"blendedFrom":[makeQuery(id+"F9.boolean.opBoolean","SPLIT",EDGE,{"disambiguationData":[TD([makeQuery(id+"F9.opExtrude","SWEPT_FACE",FACE,{"disambiguationData":[OSD([sQuery(id+"F6.wireOp",EDGE,"E130")])]})])],"derivedFrom":makeQuery(id+"F5.boolean.opBoolean","MERGE",EDGE,{"derivedFrom":[makeQuery(id+"F3.boolean.opBoolean","COPY",EDGE,{"derivedFrom":makeQuery(id+"F3.opExtrude","SWEPT_EDGE",EDGE,{"disambiguationData":[OSD([subQ2,subQ1])]})}),makeQuery(id+"F5.opExtrude","SWEPT_EDGE",EDGE,{"disambiguationData":[OSD([subQ3,subQ4])]})]})}),subQ0],"blendedInto":[subQ0]});}
            var Q10;
            Q10=makeQuery(id+"F3.boolean.opBoolean","COPY",EDGE,{"derivedFrom":makeQuery(id+"F3.opExtrude","CAP_EDGE",EDGE,{"disambiguationData":[OSD([sQuery(id+"F2.wireOp",EDGE,"E81.trimOffspring")])],"isStart":true})});
            var Q11;
            Q11=makeQuery(id+"F3.boolean.opBoolean","COPY",EDGE,{"derivedFrom":makeQuery(id+"F3.opExtrude","CAP_EDGE",EDGE,{"disambiguationData":[OSD([sQuery(id+"F2.wireOp",EDGE,"E54.trimOffspring")])],"isStart":true})});
            var Q12;
            Q12=makeQuery(id+"F3.boolean.opBoolean","COPY",EDGE,{"derivedFrom":makeQuery(id+"F3.opExtrude","CAP_EDGE",EDGE,{"disambiguationData":[OSD([sQuery(id+"F2.wireOp",EDGE,"E5.top")])],"isStart":true})});
            var Q13;
            Q13=makeQuery(id+"F3.boolean.opBoolean","COPY",EDGE,{"derivedFrom":makeQuery(id+"F3.opExtrude","CAP_EDGE",EDGE,{"disambiguationData":[OSD([sQuery(id+"F2.wireOp",EDGE,"E44.trimOffspring")])],"isStart":true})});
            var Q14;
            Q14=makeQuery(id+"F3.boolean.opBoolean","COPY",EDGE,{"derivedFrom":makeQuery(id+"F3.opExtrude","CAP_EDGE",EDGE,{"disambiguationData":[OSD([sQuery(id+"F2.wireOp",EDGE,"E39.trimOffspring")])],"isStart":true})});
            var Q15;
            Q15=makeQuery(id+"F3.boolean.opBoolean","COPY",EDGE,{"derivedFrom":makeQuery(id+"F3.opExtrude","CAP_EDGE",EDGE,{"disambiguationData":[OSD([sQuery(id+"F2.wireOp",EDGE,"E38.trimOffspring")])],"isStart":true})});
            var Q16;
            Q16=makeQuery(id+"F3.boolean.opBoolean","COPY",EDGE,{"derivedFrom":makeQuery(id+"F3.opExtrude","CAP_EDGE",EDGE,{"disambiguationData":[OSD([sQuery(id+"F2.wireOp",EDGE,"E31.trimOffspring")])],"isStart":true})});
            var Q17;
            Q17=makeQuery(id+"F3.boolean.opBoolean","COPY",EDGE,{"derivedFrom":makeQuery(id+"F3.opExtrude","CAP_EDGE",EDGE,{"disambiguationData":[OSD([sQuery(id+"F2.wireOp",EDGE,"E30.trimOffspring")])],"isStart":true})});
            var Q18;
            Q18=makeQuery(id+"F3.boolean.opBoolean","COPY",EDGE,{"derivedFrom":makeQuery(id+"F3.opExtrude","CAP_EDGE",EDGE,{"disambiguationData":[OSD([sQuery(id+"F2.wireOp",EDGE,"E5.left")])],"isStart":true})});
            fillet(context, id + "F14", {"entities" : qUnion([Q0, Q1, Q2, Q3, Q4, Q5, Q6, Q7, Q8, Q9, Q10, Q11, Q12, Q13, Q14, Q15, Q16, Q17, Q18]), "radius" : 2 * mm, "tangentPropagation" : true, "allowEdgeOverflow" : false});
        }
        {
            var Q0;
            Q0=makeQuery(id+"F1.opExtrude","CAP_FACE",FACE,{"disambiguationData":[OSD([sQuery(id+"F0.wireOp",EDGE,"E0.bottom"),sQuery(id+"F0.wireOp",EDGE,"E0.top"),sQuery(id+"F0.wireOp",EDGE,"E0.left"),sQuery(id+"F0.wireOp",EDGE,"E0.right"),sQuery(id+"F0.wireOp",EDGE,"E1.filletArc"),sQuery(id+"F0.wireOp",EDGE,"E2.filletArc"),sQuery(id+"F0.wireOp",EDGE,"E3.filletArc"),sQuery(id+"F0.wireOp",EDGE,"E4.filletArc")])],"isStart":false});
            var sketch = newSketch(context, id + "F15", { "sketchPlane" : qUnion([Q0])});
            skLineSegment(sketch, "E138.0", {"start": v(-180, 65) * mm, "end": v(180, 65) * mm});
            skLineSegment(sketch, "E139.0", {"start": v(-185, 60) * mm, "end": v(-185, -60) * mm});
            skArc(sketch, "E140.0", {"start": v(-180, 65) * mm, "mid": v(-183.54, 63.54) * mm, "end": v(-185, 60) * mm});
            skArc(sketch, "E141.0", {"start": v(-185, -60) * mm, "mid": v(-183.54, -63.54) * mm, "end": v(-180, -65) * mm});
            skLineSegment(sketch, "E142.0", {"start": v(-180, -65) * mm, "end": v(180, -65) * mm});
            skArc(sketch, "E143.0", {"start": v(180, -65) * mm, "mid": v(183.54, -63.54) * mm, "end": v(185, -60) * mm});
            skLineSegment(sketch, "E144.0", {"start": v(185, 60) * mm, "end": v(185, -60) * mm});
            skArc(sketch, "E145.0", {"start": v(-180, 67) * mm, "mid": v(-184.95, 64.95) * mm, "end": v(-187, 60) * mm});
            skLineSegment(sketch, "E145.1", {"start": v(-187, 60) * mm, "end": v(-187, -60) * mm});
            skLineSegment(sketch, "E145.2", {"start": v(-180, 67) * mm, "end": v(180, 67) * mm});
            skArc(sketch, "E145.3", {"start": v(-187, -60) * mm, "mid": v(-184.95, -64.95) * mm, "end": v(-180, -67) * mm});
            skArc(sketch, "E145.4", {"start": v(187, 60) * mm, "mid": v(184.95, 64.95) * mm, "end": v(180, 67) * mm});
            skLineSegment(sketch, "E145.5", {"start": v(187, 60) * mm, "end": v(187, -60) * mm});
            skArc(sketch, "E145.6", {"start": v(180, -67) * mm, "mid": v(184.95, -64.95) * mm, "end": v(187, -60) * mm});
            skLineSegment(sketch, "E145.7", {"start": v(-180, -67) * mm, "end": v(180, -67) * mm});
            skSolve(sketch);
        }
        {
            var Q0;
            Q0=makeQuery(id+"F15.imprint","IMPRINT",FACE,{"disambiguationData":[TD([[makeQuery(id+"F15.imprint","IMPRINT",EDGE,{"derivedFrom":sQuery(id+"F15.wireOp",EDGE,"E138.0")}),1.0]])]});
            extrude(context, id + "F16", {"entities" : qUnion([Q0]), "oppositeDirection" : true, "depth" : 1.5 * mm, "offsetDistance" : 25 * mm});
        }
    });
